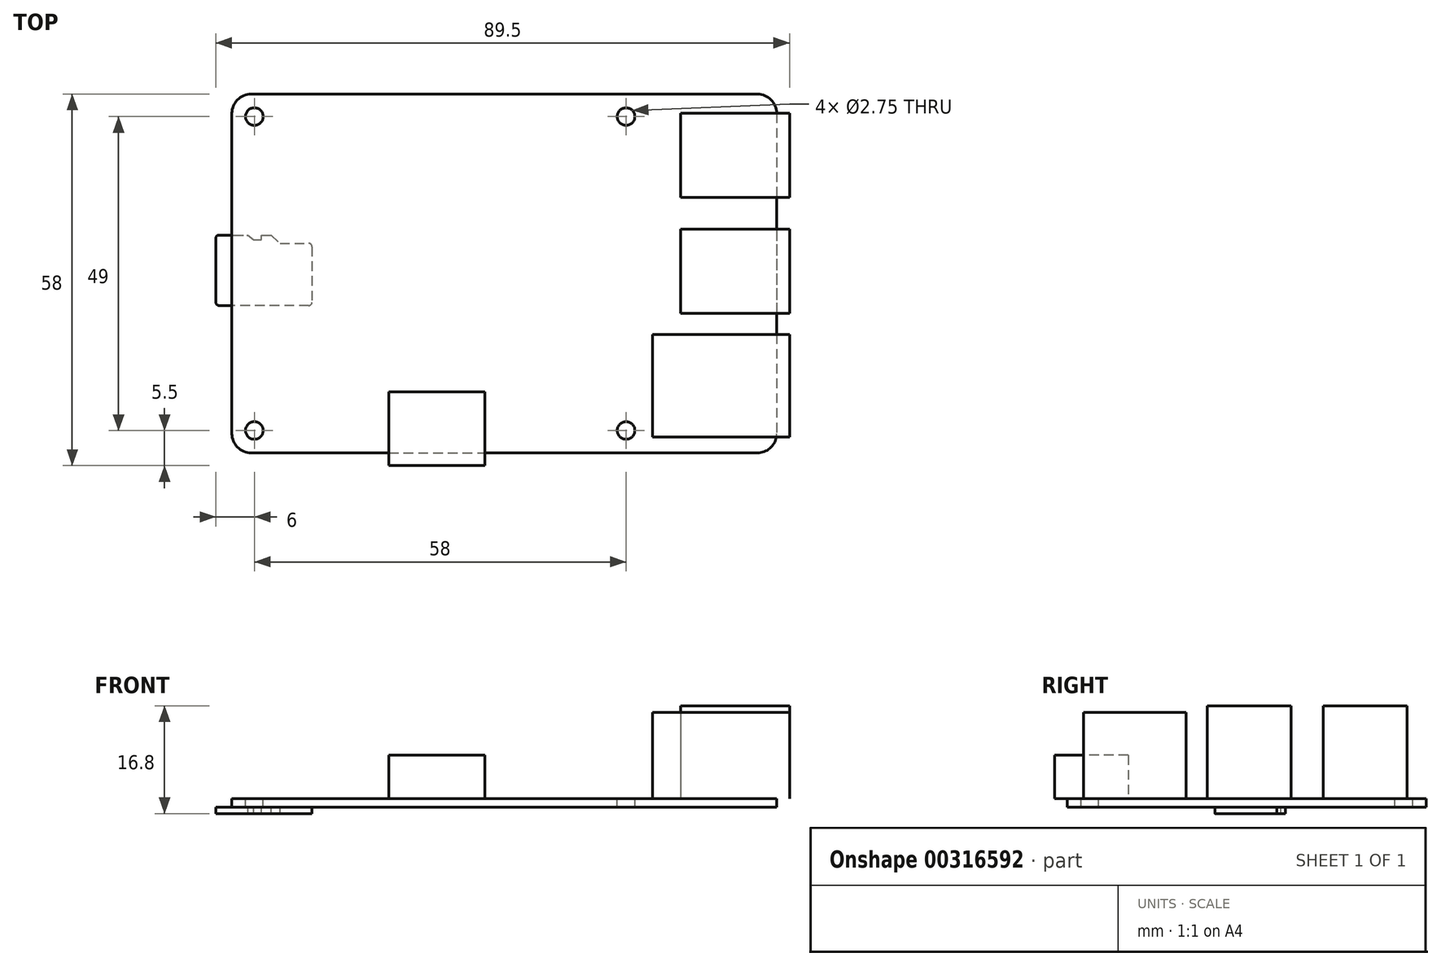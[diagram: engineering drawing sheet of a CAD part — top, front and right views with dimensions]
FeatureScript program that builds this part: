
annotation { "Feature Type Name" : "Feature", "Feature Type Description" : "" }
export const myFeature = defineFeature(function(context is Context, id is Id, definition is map)
    precondition{}
    {
        {
            var Q0;
            Q0=qCreatedBy(makeId("Top.planeOp"),FACE);
            var sketch = newSketch(context, id + "F0", { "sketchPlane" : qUnion([Q0])});
            skLineSegment(sketch, "E0.bottom", {"start": v(-39.5, 28) * mm, "end": v(39.5, 28) * mm});
            skLineSegment(sketch, "E0.top", {"start": v(-39.5, -28) * mm, "end": v(39.5, -28) * mm});
            skLineSegment(sketch, "E0.left", {"start": v(-42.5, 25) * mm, "end": v(-42.5, -25) * mm});
            skLineSegment(sketch, "E0.right", {"start": v(42.5, 25) * mm, "end": v(42.5, -25) * mm});
            skPoint(sketch, "E1", {"position": v(-42.5, 0) * mm});
            skPoint(sketch, "E2", {"position": v(0, 28) * mm});
            skPoint(sketch, "E3.visualSharp", {"position": v(-42.5, 28) * mm});
            skArc(sketch, "E3.filletArc", {"start": v(-39.5, 28) * mm, "mid": v(-41.62, 27.12) * mm, "end": v(-42.5, 25) * mm});
            skPoint(sketch, "E4.visualSharp", {"position": v(42.5, 28) * mm});
            skArc(sketch, "E4.filletArc", {"start": v(42.5, 25) * mm, "mid": v(41.62, 27.12) * mm, "end": v(39.5, 28) * mm});
            skPoint(sketch, "E5.visualSharp", {"position": v(42.5, -28) * mm});
            skArc(sketch, "E5.filletArc", {"start": v(39.5, -28) * mm, "mid": v(41.62, -27.12) * mm, "end": v(42.5, -25) * mm});
            skPoint(sketch, "E6.visualSharp", {"position": v(-42.5, -28) * mm});
            skArc(sketch, "E6.filletArc", {"start": v(-42.5, -25) * mm, "mid": v(-41.62, -27.12) * mm, "end": v(-39.5, -28) * mm});
            skSolve(sketch);
        }
        {
            var Q0;
            Q0=makeQuery(id+"F0.imprint","IMPRINT",FACE,{"disambiguationData":[TD([[makeQuery(id+"F0.imprint","IMPRINT",EDGE,{"derivedFrom":sQuery(id+"F0.wireOp",EDGE,"E0.bottom")}),-1.0]])]});
            extrude(context, id + "F1", {"entities" : qUnion([Q0]), "depth" : 1.3 * mm});
        }
        {
            var Q0;
            Q0=makeQuery(id+"F1.opExtrude","CAP_FACE",FACE,{"disambiguationData":[OSD([sQuery(id+"F0.wireOp",EDGE,"E0.bottom"),sQuery(id+"F0.wireOp",EDGE,"E0.top"),sQuery(id+"F0.wireOp",EDGE,"E0.left"),sQuery(id+"F0.wireOp",EDGE,"E0.right")])],"isStart":false});
            var sketch = newSketch(context, id + "F2", { "sketchPlane" : qUnion([Q0])});
            skCircle(sketch, "E7", {"center": v(-39, 24.5) * mm, "radius": 1.38 * mm});
            skCircle(sketch, "E8", {"center": v(19, 24.5) * mm, "radius": 1.38 * mm});
            skCircle(sketch, "E9", {"center": v(-39, -24.5) * mm, "radius": 1.38 * mm});
            skCircle(sketch, "E10", {"center": v(19, -24.5) * mm, "radius": 1.38 * mm});
            skSolve(sketch);
        }
        {
            var Q0;
            Q0=qSketchRegion(id+"F2",true);
            extrude(context, id + "F3", {"entities" : qUnion([Q0]), "operationType" : NewBodyOperationType.REMOVE, "endBound" : BoundingType.UP_TO_NEXT, "oppositeDirection" : true, "depth" : 25 * mm});
        }
        {
            var Q0;
            Q0=makeQuery(id+"F1.opExtrude","CAP_FACE",FACE,{"disambiguationData":[OSD([sQuery(id+"F0.wireOp",EDGE,"E0.bottom"),sQuery(id+"F0.wireOp",EDGE,"E0.top"),sQuery(id+"F0.wireOp",EDGE,"E0.left"),sQuery(id+"F0.wireOp",EDGE,"E0.right"),sQuery(id+"F0.wireOp",EDGE,"E3.filletArc"),sQuery(id+"F0.wireOp",EDGE,"E4.filletArc"),sQuery(id+"F0.wireOp",EDGE,"E5.filletArc"),sQuery(id+"F0.wireOp",EDGE,"E6.filletArc")])],"isStart":false});
            var sketch = newSketch(context, id + "F4", { "sketchPlane" : qUnion([Q0])});
            skLineSegment(sketch, "E11.bottom", {"start": v(23.15, -9.5) * mm, "end": v(44.5, -9.5) * mm});
            skLineSegment(sketch, "E11.top", {"start": v(23.15, -25.5) * mm, "end": v(44.5, -25.5) * mm});
            skLineSegment(sketch, "E11.left", {"start": v(23.15, -9.5) * mm, "end": v(23.15, -25.5) * mm});
            skLineSegment(sketch, "E11.right", {"start": v(44.5, -9.5) * mm, "end": v(44.5, -25.5) * mm});
            skSolve(sketch);
        }
        {
            var Q0;
            Q0=qSketchRegion(id+"F4",true);
            extrude(context, id + "F5", {"entities" : qUnion([Q0]), "flatOperationType" : FlatOperationType.REMOVE, "offsetDistance" : 25 * mm, "depth" : 13.5 * mm, "domain" : OperationDomain.MODEL});
        }
        {
            var Q0;
            Q0=makeQuery(id+"F1.opExtrude","CAP_FACE",FACE,{"disambiguationData":[OSD([sQuery(id+"F0.wireOp",EDGE,"E0.bottom"),sQuery(id+"F0.wireOp",EDGE,"E0.top"),sQuery(id+"F0.wireOp",EDGE,"E0.left"),sQuery(id+"F0.wireOp",EDGE,"E0.right"),sQuery(id+"F0.wireOp",EDGE,"E3.filletArc"),sQuery(id+"F0.wireOp",EDGE,"E4.filletArc"),sQuery(id+"F0.wireOp",EDGE,"E5.filletArc"),sQuery(id+"F0.wireOp",EDGE,"E6.filletArc")])],"isStart":false});
            var sketch = newSketch(context, id + "F6", { "sketchPlane" : qUnion([Q0])});
            skLineSegment(sketch, "E12.bottom", {"start": v(27.5, 6.9) * mm, "end": v(44.5, 6.9) * mm});
            skLineSegment(sketch, "E12.top", {"start": v(27.5, -6.2) * mm, "end": v(44.5, -6.2) * mm});
            skLineSegment(sketch, "E12.left", {"start": v(27.5, 6.9) * mm, "end": v(27.5, -6.2) * mm});
            skLineSegment(sketch, "E12.right", {"start": v(44.5, 6.9) * mm, "end": v(44.5, -6.2) * mm});
            skLineSegment(sketch, "E13.bottom", {"start": v(27.5, 25) * mm, "end": v(44.5, 25) * mm});
            skLineSegment(sketch, "E13.top", {"start": v(27.5, 11.9) * mm, "end": v(44.5, 11.9) * mm});
            skLineSegment(sketch, "E13.left", {"start": v(27.5, 25) * mm, "end": v(27.5, 11.9) * mm});
            skLineSegment(sketch, "E13.right", {"start": v(44.5, 25) * mm, "end": v(44.5, 11.9) * mm});
            skSolve(sketch);
        }
        {
            var Q0;
            Q0=qSketchRegion(id+"F6",true);
            extrude(context, id + "F7", {"entities" : qUnion([Q0]), "depth" : 14.5 * mm});
        }
        {
            var Q0;
            Q0=makeQuery(id+"F1.opExtrude","CAP_FACE",FACE,{"disambiguationData":[OSD([sQuery(id+"F0.wireOp",EDGE,"E0.bottom"),sQuery(id+"F0.wireOp",EDGE,"E0.top"),sQuery(id+"F0.wireOp",EDGE,"E0.left"),sQuery(id+"F0.wireOp",EDGE,"E0.right"),sQuery(id+"F0.wireOp",EDGE,"E3.filletArc"),sQuery(id+"F0.wireOp",EDGE,"E4.filletArc"),sQuery(id+"F0.wireOp",EDGE,"E5.filletArc"),sQuery(id+"F0.wireOp",EDGE,"E6.filletArc")])],"isStart":false});
            var sketch = newSketch(context, id + "F8", { "sketchPlane" : qUnion([Q0])});
            skLineSegment(sketch, "E14.bottom", {"start": v(-18, -18.5) * mm, "end": v(-3, -18.5) * mm});
            skLineSegment(sketch, "E14.top", {"start": v(-18, -30) * mm, "end": v(-3, -30) * mm});
            skLineSegment(sketch, "E14.left", {"start": v(-18, -18.5) * mm, "end": v(-18, -30) * mm});
            skLineSegment(sketch, "E14.right", {"start": v(-3, -18.5) * mm, "end": v(-3, -30) * mm});
            skPoint(sketch, "E15", {"position": v(-10.5, -30) * mm});
            skSolve(sketch);
        }
        {
            var Q0;
            Q0=qSketchRegion(id+"F8",true);
            extrude(context, id + "F9", {"entities" : qUnion([Q0]), "depth" : 6.8 * mm});
        }
        {
            var Q0;
            Q0=makeQuery(id+"F1.opExtrude","CAP_FACE",FACE,{"disambiguationData":[OSD([sQuery(id+"F0.wireOp",EDGE,"E0.bottom"),sQuery(id+"F0.wireOp",EDGE,"E0.top"),sQuery(id+"F0.wireOp",EDGE,"E0.left"),sQuery(id+"F0.wireOp",EDGE,"E0.right"),sQuery(id+"F0.wireOp",EDGE,"E3.filletArc"),sQuery(id+"F0.wireOp",EDGE,"E4.filletArc"),sQuery(id+"F0.wireOp",EDGE,"E5.filletArc"),sQuery(id+"F0.wireOp",EDGE,"E6.filletArc")])],"isStart":true});
            var sketch = newSketch(context, id + "F10", { "sketchPlane" : qUnion([Q0])});
            skLineSegment(sketch, "E16", {"start": v(-45, 4.5) * mm, "end": v(-45, -5.5) * mm});
            skLineSegment(sketch, "E17", {"start": v(-44.5, -6) * mm, "end": v(-40, -6) * mm});
            skLineSegment(sketch, "E18", {"start": v(-40, -6) * mm, "end": v(-39.1, -5.3) * mm});
            skLineSegment(sketch, "E19", {"start": v(-39.1, -5.3) * mm, "end": v(-37.9, -5.3) * mm});
            skLineSegment(sketch, "E20", {"start": v(-37.9, -5.3) * mm, "end": v(-37.9, -6) * mm});
            skLineSegment(sketch, "E21", {"start": v(-37.9, -6) * mm, "end": v(-36.4, -6) * mm});
            skLineSegment(sketch, "E22", {"start": v(-36.4, -6) * mm, "end": v(-35, -4.7) * mm});
            skLineSegment(sketch, "E23", {"start": v(-35, -4.7) * mm, "end": v(-30.5, -4.7) * mm});
            skLineSegment(sketch, "E24", {"start": v(-30, -4.2) * mm, "end": v(-30, 4.5) * mm});
            skLineSegment(sketch, "E25", {"start": v(-30.5, 5) * mm, "end": v(-44.5, 5) * mm});
            skPoint(sketch, "E26.visualSharp", {"position": v(-45, 5) * mm});
            skArc(sketch, "E26.filletArc", {"start": v(-44.5, 5) * mm, "mid": v(-44.85, 4.85) * mm, "end": v(-45, 4.5) * mm});
            skPoint(sketch, "E27.visualSharp", {"position": v(-30, 5) * mm});
            skArc(sketch, "E27.filletArc", {"start": v(-30, 4.5) * mm, "mid": v(-30.15, 4.85) * mm, "end": v(-30.5, 5) * mm});
            skPoint(sketch, "E28.visualSharp", {"position": v(-30, -4.7) * mm});
            skArc(sketch, "E28.filletArc", {"start": v(-30.5, -4.7) * mm, "mid": v(-30.15, -4.55) * mm, "end": v(-30, -4.2) * mm});
            skPoint(sketch, "E29.visualSharp", {"position": v(-45, -6) * mm});
            skArc(sketch, "E29.filletArc", {"start": v(-45, -5.5) * mm, "mid": v(-44.85, -5.85) * mm, "end": v(-44.5, -6) * mm});
            skSolve(sketch);
        }
        {
            var Q0;
            Q0=qSketchRegion(id+"F10",true);
            extrude(context, id + "F11", {"entities" : qUnion([Q0]), "depth" : 1 * mm});
        }
    });
